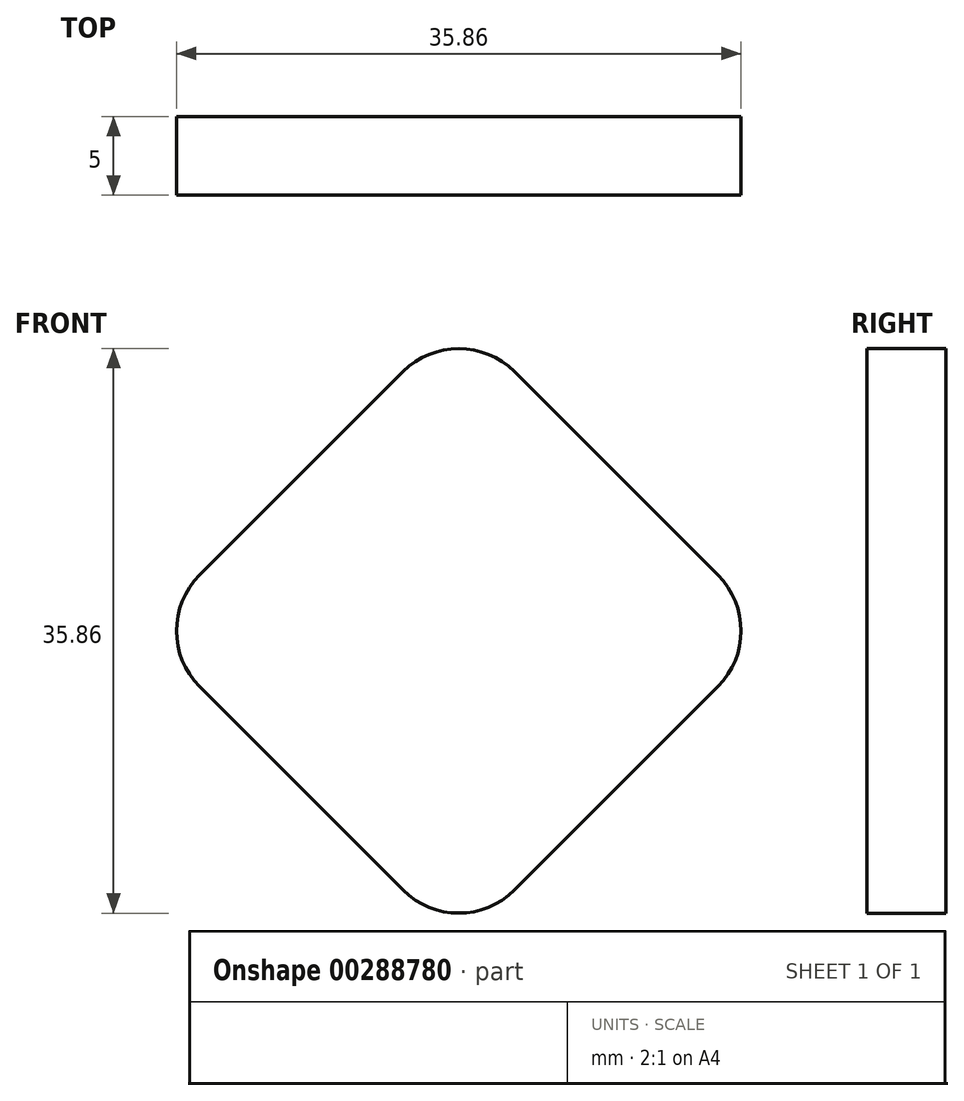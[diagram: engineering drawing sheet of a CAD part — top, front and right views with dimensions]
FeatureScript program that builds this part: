
annotation { "Feature Type Name" : "Feature", "Feature Type Description" : "" }
export const myFeature = defineFeature(function(context is Context, id is Id, definition is map)
    precondition{}
    {
        {
            var Q0;
            Q0=qCreatedBy(makeId("Front.planeOp"),FACE);
            var sketch = newSketch(context, id + "F0", { "sketchPlane" : qUnion([Q0])});
            skPoint(sketch, "E0.middle", {"position": v(0, 0) * mm});
            skLineSegment(sketch, "E1", {"start": v(-16.46, 3.54) * mm, "end": v(-3.54, 16.46) * mm});
            skLineSegment(sketch, "E2", {"start": v(3.54, 16.46) * mm, "end": v(16.46, 3.54) * mm});
            skLineSegment(sketch, "E3", {"start": v(16.46, -3.54) * mm, "end": v(3.54, -16.46) * mm});
            skLineSegment(sketch, "E4", {"start": v(-3.54, -16.46) * mm, "end": v(-16.46, -3.54) * mm});
            skPoint(sketch, "E5.visualSharp", {"position": v(0, 20) * mm});
            skArc(sketch, "E5.filletArc", {"start": v(3.54, 16.46) * mm, "mid": v(0, 17.93) * mm, "end": v(-3.54, 16.46) * mm});
            skPoint(sketch, "E6.visualSharp", {"position": v(20, 0) * mm});
            skArc(sketch, "E6.filletArc", {"start": v(16.46, -3.54) * mm, "mid": v(17.93, 0) * mm, "end": v(16.46, 3.54) * mm});
            skPoint(sketch, "E7.visualSharp", {"position": v(0, -20) * mm});
            skArc(sketch, "E7.filletArc", {"start": v(-3.54, -16.46) * mm, "mid": v(0, -17.93) * mm, "end": v(3.54, -16.46) * mm});
            skPoint(sketch, "E8.visualSharp", {"position": v(-20, 0) * mm});
            skArc(sketch, "E8.filletArc", {"start": v(-16.46, 3.54) * mm, "mid": v(-17.93, 0) * mm, "end": v(-16.46, -3.54) * mm});
            skSolve(sketch);
        }
        {
            var Q0;
            Q0=makeQuery(id+"F0.imprint","IMPRINT",FACE,{"disambiguationData":[TD([[makeQuery(id+"F0.imprint","IMPRINT",EDGE,{"derivedFrom":sQuery(id+"F0.wireOp",EDGE,"E1")}),-1.0]])]});
            extrude(context, id + "F1", {"entities" : qUnion([Q0]), "depth" : 5 * mm});
        }
    });
